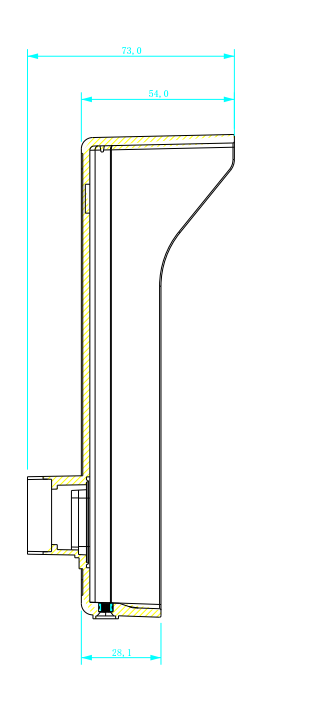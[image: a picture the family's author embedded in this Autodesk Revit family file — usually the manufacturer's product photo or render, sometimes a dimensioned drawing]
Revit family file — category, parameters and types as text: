
# Revit family: UPS-DP_F
name_source: partatom
category: Устройства связи
units: mm (PartAtom-declared; Revit-internal decimal feet)

## family parameters
Всегда вертикально = Нет
На основе рабочей плоскости = Да
Общий = Да
При загрузке вырезать с полостями = Нет
Размер круглого соединителя = Использовать диаметр
Сохранять ориентацию аннотаций = Нет
Тип детали = Нормальный
Точка расчета площади = Нет

## types (1)
- UPS-DP/F
    ADSK_URL документации изделия = https://drive.google.com
    ADSK_URL страницы изделия = https://bas-ip.com
    ADSK_Версия Revit = Revit 2020
    ADSK_Единица измерения = шт
    ADSK_Завод-изготовитель = BAS-IP
    ADSK_Классификация нагрузок = Блок бесперебойного питания
    ADSK_Количество фаз = 1
    ADSK_Коэффициент мощности = 0.9
    ADSK_Марка = UPS-DP/F
    ADSK_Наименование = Блок бесперебойного питания UPS-DP/F
    ADSK_Наименование краткое = UPS-DP/F
    ADSK_Напряжение = 12 В
    ADSK_Номинальная мощность = 0 Вт
    ADSK_Полная мощность = 4 В·А
    ADSK_Размер_Длина = 190 мм
    ADSK_Размер_Толщина = 72 мм
    ADSK_Размер_Ширина = 180 мм
    BIM library = https://bimlib.ru
    URL = https://www.bas-ip.ru
    Вес брутто = 1,27 кг
    Входное напряжение = 100-230 В переменного тока
    Выходное напряжение = +12 В
    Габаритные размеры = 180×190×72 мм
    Группа модели = Блок бесперебойного питания UPS-DP/F
    Изготовитель = BAS-IP
    Изображение типоразмера = <Нет>
    Класс защиты = IP30C
    Максимальный кратковременный ток нагрузки = 3,5 А
    Материал корпуса = Материал черный
    Описание = Блок бесперебойного питания (ИБП) для многоквартирных вызывных панелей со встроенным управлением электромагнитным и электромеханическим замком. Его также можно использовать с отдельными панелями или монитором консьержа.
    Отметка по умолчанию = 0 мм
    Рабочая температура = -40 – +60 ℃
    Тип корпуса = Металлический
    Тип подключаемого оборудования = Многоабонентская вызывная панель
